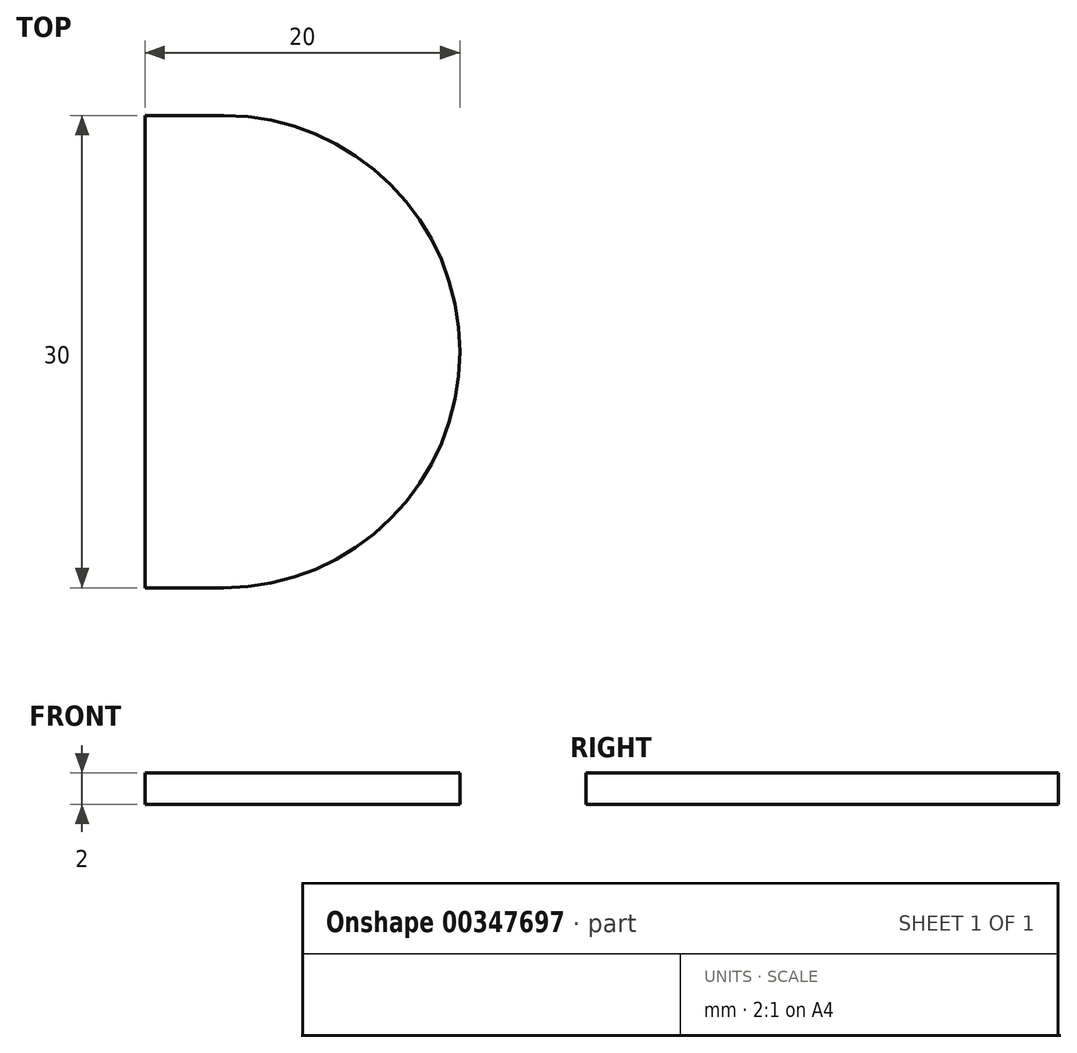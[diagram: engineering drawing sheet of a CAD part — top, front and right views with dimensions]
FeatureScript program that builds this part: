
annotation { "Feature Type Name" : "Feature", "Feature Type Description" : "" }
export const myFeature = defineFeature(function(context is Context, id is Id, definition is map)
    precondition{}
    {
        {
            var Q0;
            Q0=qCreatedBy(makeId("Top.planeOp"),FACE);
            var sketch = newSketch(context, id + "F0", { "sketchPlane" : qUnion([Q0])});
            skLineSegment(sketch, "E0", {"start": v(-19.35, -20594.19) * mm, "end": v(0.65, -20594.19) * mm});
            skLineSegment(sketch, "E1", {"start": v(0.65, -20594.19) * mm, "end": v(0.65, -20624.19) * mm});
            skLineSegment(sketch, "E2", {"start": v(0.65, -20624.19) * mm, "end": v(-19.35, -20624.19) * mm});
            skLineSegment(sketch, "E3", {"start": v(-19.35, -20624.19) * mm, "end": v(-19.35, -20594.19) * mm});
            skSolve(sketch);
        }
        {
            var Q0;
            Q0 = qSketchRegion(id + "F0", true);
            extrude(context, id + "F1", {"entities" : qUnion([Q0]), "depth" : 2 * mm});
        }
        {
            var Q0;
            Q0=makeQuery(id+"F1.opExtrude","SWEPT_EDGE",EDGE,{"disambiguationData":[OSD([sQuery(id+"F0.wireOp",EDGE,"E0"),sQuery(id+"F0.wireOp",EDGE,"E1")])]});
            var Q1;
            Q1=makeQuery(id+"F1.opExtrude","SWEPT_EDGE",EDGE,{"disambiguationData":[OSD([sQuery(id+"F0.wireOp",EDGE,"E1"),sQuery(id+"F0.wireOp",EDGE,"E2")])]});
            fillet(context, id + "F2", {"entities" : qUnion([Q0, Q1]), "radius" : 15 * mm, "tangentPropagation" : true, "allowEdgeOverflow" : false});
        }
    });
